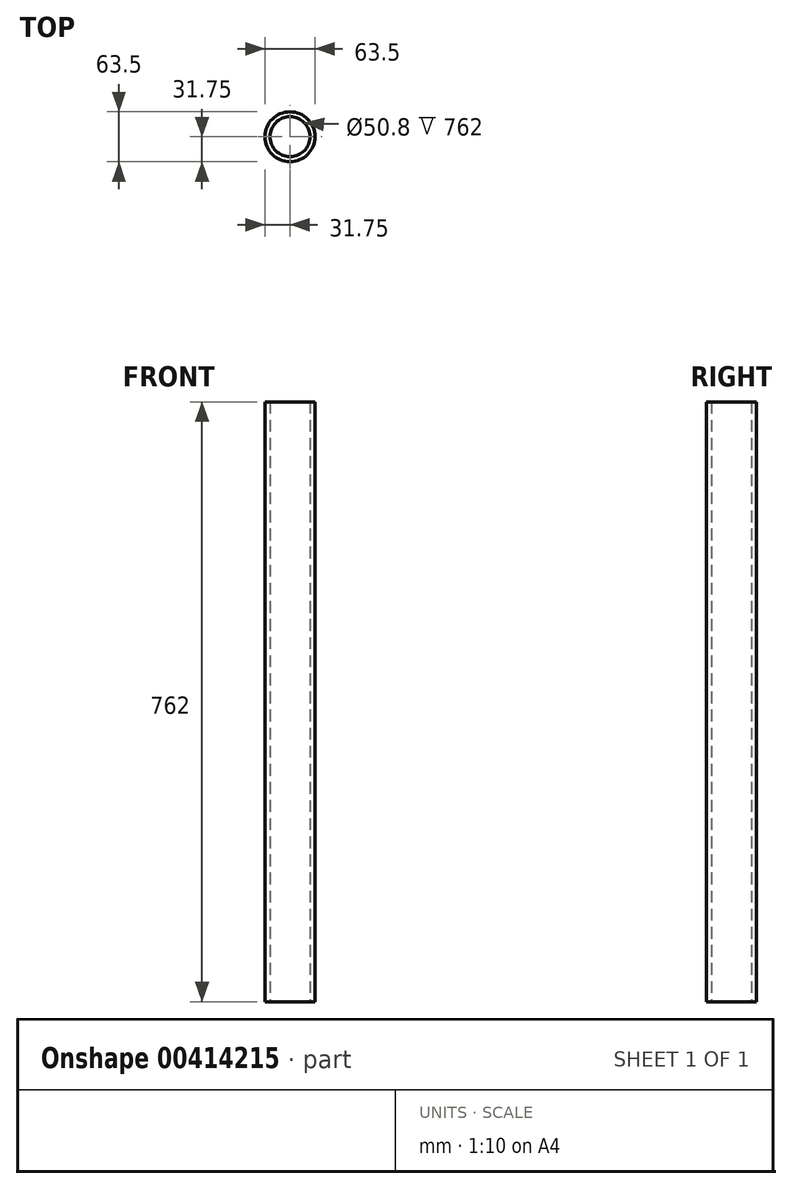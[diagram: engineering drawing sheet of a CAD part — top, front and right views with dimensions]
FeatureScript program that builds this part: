
annotation { "Feature Type Name" : "Feature", "Feature Type Description" : "" }
export const myFeature = defineFeature(function(context is Context, id is Id, definition is map)
    precondition{}
    {
        {
            var Q0;
            Q0=qCreatedBy(makeId("Top.planeOp"),FACE);
            var sketch = newSketch(context, id + "F0", { "sketchPlane" : qUnion([Q0])});
            skCircle(sketch, "E0", {"center": v(0, 0) * mm, "radius": 31.75 * mm});
            skCircle(sketch, "E1", {"center": v(0, 0) * mm, "radius": 25.4 * mm});
            skSolve(sketch);
        }
        {
            var Q0;
            Q0=makeQuery(id+"F0.imprint","IMPRINT",FACE,{"disambiguationData":[TD([[makeQuery(id+"F0.imprint","IMPRINT",EDGE,{"derivedFrom":sQuery(id+"F0.wireOp",EDGE,"E0")}),1.0]])]});
            extrude(context, id + "F1", {"entities" : qUnion([Q0]), "depth" : 762 * mm});
        }
    });
